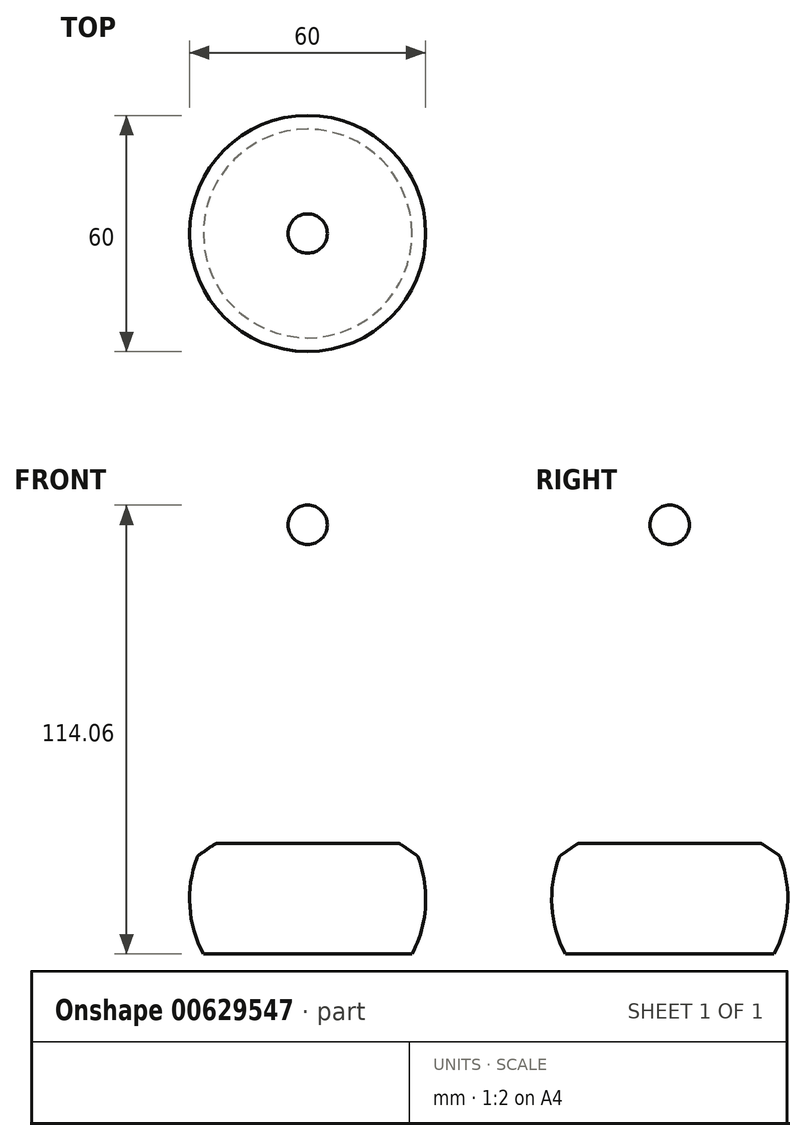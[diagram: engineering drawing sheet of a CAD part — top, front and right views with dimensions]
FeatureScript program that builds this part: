
annotation { "Feature Type Name" : "Feature", "Feature Type Description" : "" }
export const myFeature = defineFeature(function(context is Context, id is Id, definition is map)
    precondition{}
    {
        {
            var Q0;
            Q0=qCreatedBy(makeId("Front.planeOp"),FACE);
            var sketch = newSketch(context, id + "F0", { "sketchPlane" : qUnion([Q0])});
            skArc(sketch, "E0", {"start": v(0, -100) * mm, "mid": v(100, 0) * mm, "end": v(0, 100) * mm});
            skLineSegment(sketch, "E1", {"start": v(0, 115.41) * mm, "end": v(0, -116.3) * mm});
            skArc(sketch, "E2", {"start": v(26.5, -14.06) * mm, "mid": v(30, 0) * mm, "end": v(26.5, 14.06) * mm});
            skLineSegment(sketch, "E3", {"start": v(0, 14.06) * mm, "end": v(26.5, 14.06) * mm});
            skLineSegment(sketch, "E4", {"start": v(0, -14.06) * mm, "end": v(26.5, -14.06) * mm});
            skArc(sketch, "E5", {"start": v(0, 90) * mm, "mid": v(5, 95) * mm, "end": v(0, 100) * mm});
            skSolve(sketch);
        }
        {
            var Q0;
            Q0=sQuery(id+"F0.wireOp",EDGE,"E0");
            var Q1;
            Q1=sQuery(id+"F0.wireOp",EDGE,"E1");
            revolve(context, id + "F1", {"bodyType" : ToolBodyType.SURFACE, "surfaceEntities" : qUnion([Q0]), "axis" : qUnion([Q1]), "revolveType" : RevolveType.FULL});
        }
        {
            var Q0;
            Q0=makeQuery(id+"F0.imprint","IMPRINT",FACE,{"disambiguationData":[TD([[makeQuery(id+"F0.imprint","IMPRINT",EDGE,{"derivedFrom":sQuery(id+"F0.wireOp",EDGE,"E2")}),1.0]])]});
            var Q1;
            Q1=sQuery(id+"F0.wireOp",EDGE,"E1");
            revolve(context, id + "F2", {"entities" : qUnion([Q0]), "axis" : qUnion([Q1]), "revolveType" : RevolveType.FULL});
        }
        {
            var Q0;
            Q0=makeQuery(id+"F2.opRevolve","SWEPT_EDGE",EDGE,{"disambiguationData":[OSD([sQuery(id+"F0.wireOp",EDGE,"E2"),sQuery(id+"F0.wireOp",EDGE,"E3")])]});
            chamfer(context, id + "F3", {"entities" : qUnion([Q0]), "width" : 5 * mm, "tangentPropagation" : true});
        }
        {
            var Q0;
            {var subQ0=sQuery(id+"F0.wireOp",EDGE,"E3");Q0=makeQuery(id+"F3.opChamfer","BLEND_EDGE",EDGE,{"blendedFrom":[makeQuery(id+"F2.opRevolve","SWEPT_EDGE",EDGE,{"disambiguationData":[OSD([sQuery(id+"F0.wireOp",EDGE,"E2"),subQ0])]}),makeQuery(id+"F2.opRevolve","SWEPT_FACE",FACE,{"disambiguationData":[OSD([subQ0])]})],"blendedInto":[makeQuery(id+"F2.opRevolve","SWEPT_FACE",FACE,{"disambiguationData":[OSD([subQ0])]})]});}
            fillet(context, id + "F4", {"entities" : qUnion([Q0]), "radius" : 1.5 * mm, "tangentPropagation" : true, "allowEdgeOverflow" : false});
        }
        {
            var Q0;
            {var subQ0=sQuery(id+"F0.wireOp",EDGE,"E2");Q0=makeQuery(id+"F3.opChamfer","BLEND_EDGE",EDGE,{"blendedFrom":[makeQuery(id+"F2.opRevolve","SWEPT_EDGE",EDGE,{"disambiguationData":[OSD([subQ0,sQuery(id+"F0.wireOp",EDGE,"E3")])]}),makeQuery(id+"F2.opRevolve","SWEPT_FACE",FACE,{"disambiguationData":[OSD([subQ0])]})],"blendedInto":[makeQuery(id+"F2.opRevolve","SWEPT_FACE",FACE,{"disambiguationData":[OSD([subQ0])]})]});}
            fillet(context, id + "F5", {"entities" : qUnion([Q0]), "radius" : 1.5 * mm, "tangentPropagation" : true, "allowEdgeOverflow" : false});
        }
        {
            var Q0;
            Q0=qCreatedBy(makeId("Front.planeOp"),FACE);
            var Q1;
            Q1=sQuery(id+"F0.wireOp",EDGE,"E1");
            cPlane(context, id + "F6", {"entities" : qUnion([Q0, Q1]), "cplaneType" : CPlaneType.LINE_ANGLE, "offset" : 25 * mm, "angle" : 120 * degree, "width" : 150 * mm, "height" : 150 * mm});
        }
        {
            var Q0;
            {var subQ0=sQuery(id+"F0.wireOp",EDGE,"E5");Q0=makeQuery(id+"F0.imprint","IMPRINT",FACE,{"disambiguationData":[TD([[makeQuery(id+"F0.imprint","IMPRINT",EDGE,{"derivedFrom":subQ0}),1.0]])]});}
            var Q1;
            Q1=sQuery(id+"F0.wireOp",EDGE,"E1");
            revolve(context, id + "F7", {"entities" : qUnion([Q0]), "axis" : qUnion([Q1]), "revolveType" : RevolveType.FULL});
        }
    });
